# Revit family: QF_ELECTROLUXPROFESSIONAL_206353_LIFT9E
name_source: partatom
category: Specialty Equipment
units: mm (PartAtom-declared; Revit-internal decimal feet)

## family parameters
Always vertical = Yes
Cut with Voids When Loaded = No
Enable Cutting in Views = No
Maintain Annotation Orientation = No
Part Type = Normal
Room Calculation Point = No
Round Connector Dimension = Use Diameter
Shared = No
Work Plane-Based = No

## types (1)
- QF_ELECTROLUXPROFESSIONAL_206353_LIFT9E
    Apparent Power = 0 VA
    Conn Conduit = Yes
    Default Elevation = 0 mm  [stored 0 ft]
    Depth = 930 mm  [stored 3.05118 ft]
    Description = AUTOMATIC PROGRAMMABLE BASKET LIFTING SYSTEM FOR 40LT PASTA COOKERS, 3 LIFTERS
    Direct Waste Size = 0"
    FL Amps = 0 A
    HP = 0.3 HP
    Height = 850 mm  [stored 2.78871 ft]
    Manufacturer = ELECTROLUX
    Max Overcurrent Protection = 0 A
    Min Ckt Ampacity = 0 A
    Model = 206353
    Phase = 1
    URL = www.electrolux.com
    URL Cutsheet = www.electrolux.com
    Volts = 230 V
    Watts = 0 W
    Weight in Pounds = 40
    Width = 200 mm  [stored 0.656168 ft]

note: [stored X ft] marks values corroborated as IEEE doubles in the binary element streams (Revit-internal decimal feet)

## geometry (parser evidence)
native form markers: Blend x4, Sweep x1
no freeform markers — native parametric forms only
